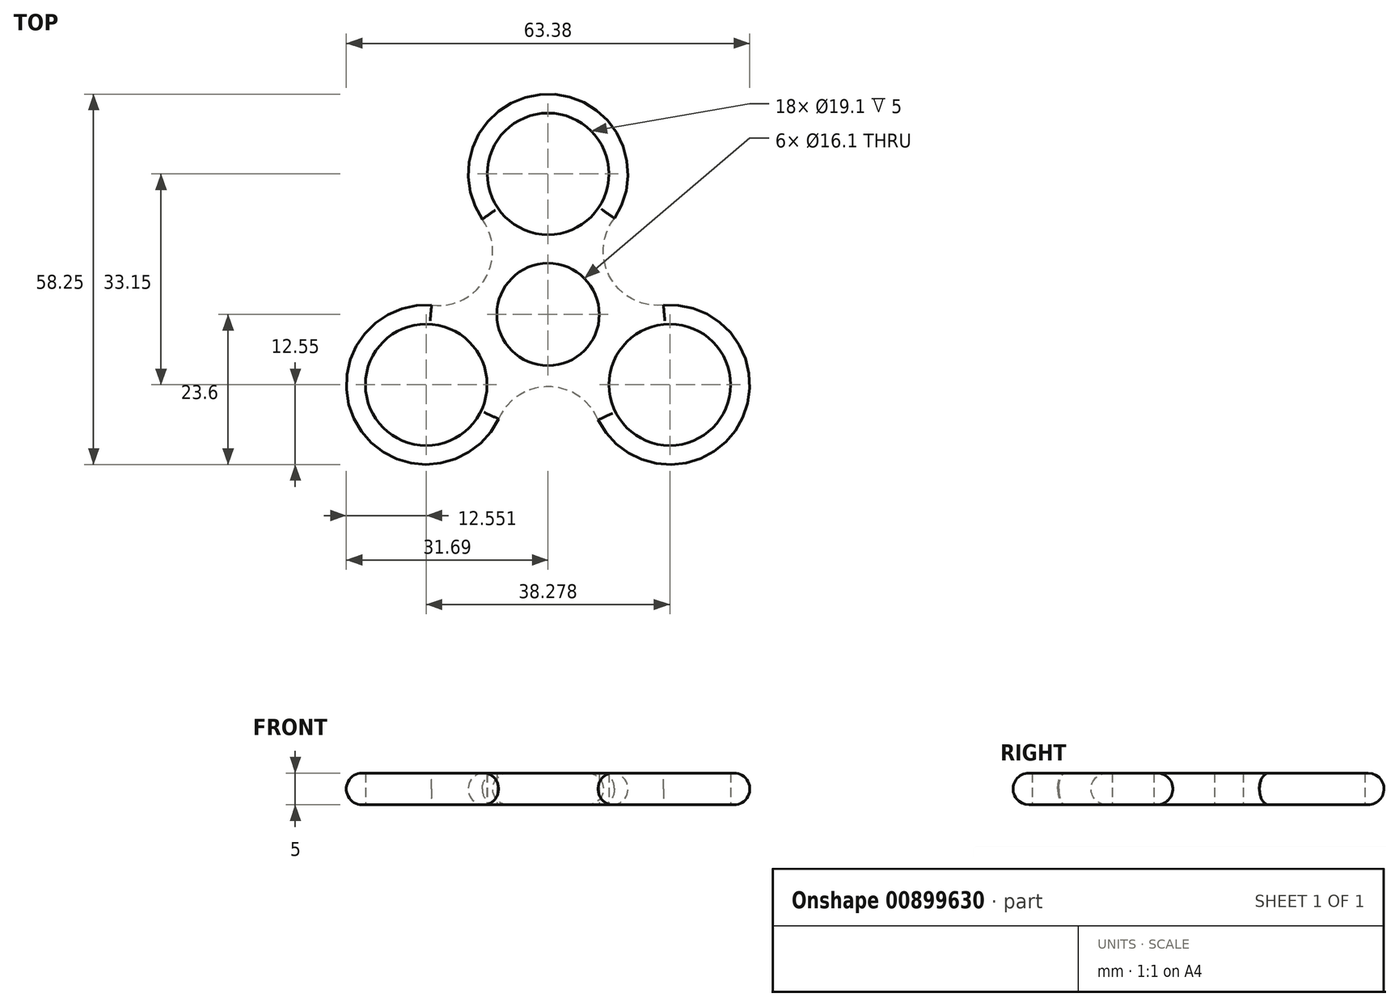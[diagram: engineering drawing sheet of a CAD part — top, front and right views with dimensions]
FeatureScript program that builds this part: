
annotation { "Feature Type Name" : "Feature", "Feature Type Description" : "" }
export const myFeature = defineFeature(function(context is Context, id is Id, definition is map)
    precondition{}
    {
        {
            var Q0;
            Q0=qCreatedBy(makeId("Top.planeOp"),FACE);
            var sketch = newSketch(context, id + "F0", { "sketchPlane" : qUnion([Q0])});
            skCircle(sketch, "E0", {"center": v(0, 0) * mm, "radius": 8.05 * mm});
            skCircle(sketch, "E1", {"center": v(0, 22.1) * mm, "radius": 9.55 * mm});
            skCircle(sketch, "E2.0", {"center": v(0, 22.1) * mm, "radius": 12.55 * mm});
            skPoint(sketch, "E3.center", {"position": v(-0.13, -6.77) * mm});
            skPoint(sketch, "E4.center", {"position": v(-0.64, -0.65) * mm});
            skCircle(sketch, "E5", {"center": v(0, 0) * mm, "radius": 20.6 * mm, "construction": true});
            skPoint(sketch, "E6.center", {"position": v(0, -1) * mm});
            skCircle(sketch, "E7.1.0", {"center": v(-19.14, -11.05) * mm, "radius": 9.55 * mm});
            skCircle(sketch, "E7.1.1", {"center": v(-19.14, -11.05) * mm, "radius": 12.55 * mm});
            skCircle(sketch, "E7.2.0", {"center": v(19.14, -11.05) * mm, "radius": 9.55 * mm});
            skCircle(sketch, "E7.2.1", {"center": v(19.14, -11.05) * mm, "radius": 12.55 * mm});
            skArc(sketch, "E8", {"start": v(10.42, 15.1) * mm, "mid": v(9.79, 5.76) * mm, "end": v(18.12, 1.46) * mm});
            skArc(sketch, "E9.1.0", {"start": v(-18.3, 1.47) * mm, "mid": v(-9.88, 5.6) * mm, "end": v(-10.32, 14.96) * mm});
            skArc(sketch, "E9.2.0", {"start": v(7.87, -16.58) * mm, "mid": v(0.1, -11.35) * mm, "end": v(-7.8, -16.42) * mm});
            skSolve(sketch);
        }
        {
            var Q0;
            Q0=makeQuery(id+"F0.imprint","IMPRINT",FACE,{"disambiguationData":[TD([[makeQuery(id+"F0.imprint","IMPRINT",EDGE,{"derivedFrom":sQuery(id+"F0.wireOp",EDGE,"E0")}),-1.0]])]});
            var Q1;
            Q1=makeQuery(id+"F0.imprint","IMPRINT",FACE,{"disambiguationData":[TD([[makeQuery(id+"F0.imprint","IMPRINT",EDGE,{"derivedFrom":sQuery(id+"F0.wireOp",EDGE,"E1")}),-1.0]])]});
            var Q2;
            Q2=makeQuery(id+"F0.imprint","IMPRINT",FACE,{"disambiguationData":[TD([[makeQuery(id+"F0.imprint","IMPRINT",EDGE,{"derivedFrom":sQuery(id+"F0.wireOp",EDGE,"E7.2.0")}),-1.0]])]});
            var Q3;
            Q3=makeQuery(id+"F0.imprint","IMPRINT",FACE,{"disambiguationData":[TD([[makeQuery(id+"F0.imprint","IMPRINT",EDGE,{"derivedFrom":sQuery(id+"F0.wireOp",EDGE,"E7.1.0")}),-1.0]])]});
            extrude(context, id + "F1", {"entities" : qUnion([Q0, Q1, Q2, Q3]), "depth" : 5 * mm, "offsetDistance" : 25 * mm});
        }
        {
            var Q0;
            Q0=makeQuery(id+"F1.opExtrude","CAP_EDGE",EDGE,{"disambiguationData":[OSD([sQuery(id+"F0.wireOp",EDGE,"E9.1.0")])],"isStart":true});
            var Q1;
            Q1=makeQuery(id+"F1.opExtrude","CAP_EDGE",EDGE,{"disambiguationData":[OSD([sQuery(id+"F0.wireOp",EDGE,"E2.0")])],"isStart":true});
            var Q2;
            Q2=makeQuery(id+"F1.opExtrude","CAP_EDGE",EDGE,{"disambiguationData":[OSD([sQuery(id+"F0.wireOp",EDGE,"E8")])],"isStart":true});
            var Q3;
            Q3=makeQuery(id+"F1.opExtrude","CAP_EDGE",EDGE,{"disambiguationData":[OSD([sQuery(id+"F0.wireOp",EDGE,"E7.2.1")])],"isStart":true});
            var Q4;
            Q4=makeQuery(id+"F1.opExtrude","CAP_EDGE",EDGE,{"disambiguationData":[OSD([sQuery(id+"F0.wireOp",EDGE,"E9.2.0")])],"isStart":true});
            var Q5;
            Q5=makeQuery(id+"F1.opExtrude","CAP_EDGE",EDGE,{"disambiguationData":[OSD([sQuery(id+"F0.wireOp",EDGE,"E7.1.1")])],"isStart":true});
            var Q6;
            Q6=makeQuery(id+"F1.opExtrude","CAP_EDGE",EDGE,{"disambiguationData":[OSD([sQuery(id+"F0.wireOp",EDGE,"E2.0")])],"isStart":false});
            var Q7;
            Q7=makeQuery(id+"F1.opExtrude","CAP_EDGE",EDGE,{"disambiguationData":[OSD([sQuery(id+"F0.wireOp",EDGE,"E8")])],"isStart":false});
            var Q8;
            Q8=makeQuery(id+"F1.opExtrude","CAP_EDGE",EDGE,{"disambiguationData":[OSD([sQuery(id+"F0.wireOp",EDGE,"E7.2.1")])],"isStart":false});
            var Q9;
            Q9=makeQuery(id+"F1.opExtrude","CAP_EDGE",EDGE,{"disambiguationData":[OSD([sQuery(id+"F0.wireOp",EDGE,"E9.2.0")])],"isStart":false});
            var Q10;
            Q10=makeQuery(id+"F1.opExtrude","CAP_EDGE",EDGE,{"disambiguationData":[OSD([sQuery(id+"F0.wireOp",EDGE,"E7.1.1")])],"isStart":false});
            var Q11;
            Q11=makeQuery(id+"F1.opExtrude","CAP_EDGE",EDGE,{"disambiguationData":[OSD([sQuery(id+"F0.wireOp",EDGE,"E9.1.0")])],"isStart":false});
            fillet(context, id + "F2", {"entities" : qUnion([Q0, Q1, Q2, Q3, Q4, Q5, Q6, Q7, Q8, Q9, Q10, Q11]), "radius" : 2.5 * mm, "tangentPropagation" : true, "allowEdgeOverflow" : false});
        }
    });
